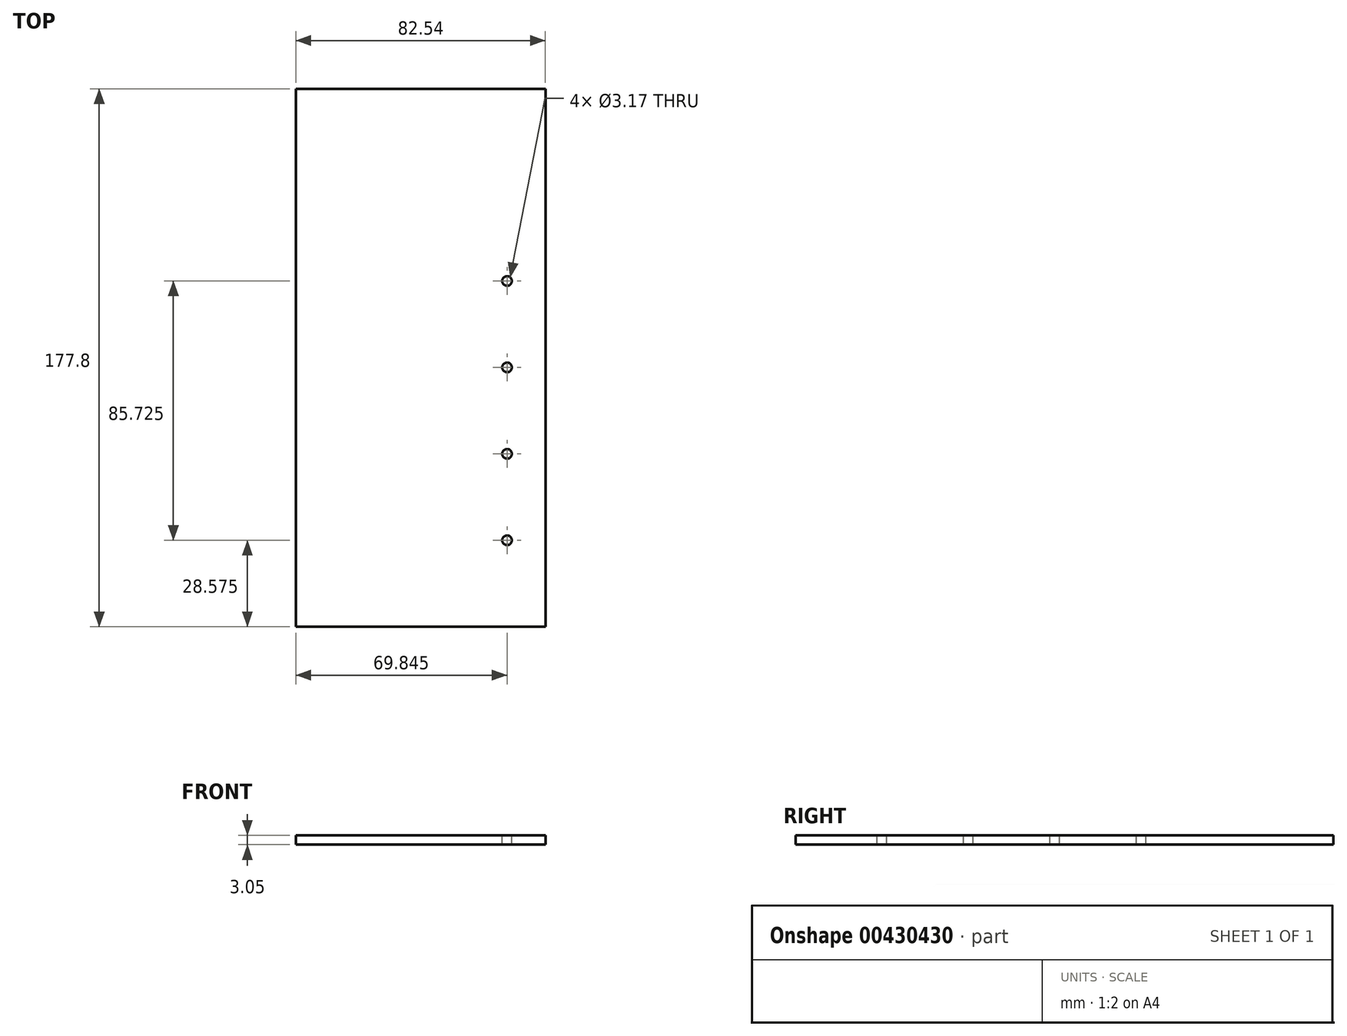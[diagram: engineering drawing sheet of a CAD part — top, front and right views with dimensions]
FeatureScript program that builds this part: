
annotation { "Feature Type Name" : "Feature", "Feature Type Description" : "" }
export const myFeature = defineFeature(function(context is Context, id is Id, definition is map)
    precondition{}
    {
        {
            var Q0;
            Q0=qCreatedBy(makeId("Top.planeOp"),FACE);
            var sketch = newSketch(context, id + "F0", { "sketchPlane" : qUnion([Q0])});
            skLineSegment(sketch, "E0.bottom", {"start": v(41.28, -88.9) * mm, "end": v(-41.27, -88.9) * mm});
            skLineSegment(sketch, "E0.top", {"start": v(41.27, 88.9) * mm, "end": v(-41.28, 88.9) * mm});
            skLineSegment(sketch, "E0.left", {"start": v(41.28, -88.9) * mm, "end": v(41.27, 88.9) * mm});
            skLineSegment(sketch, "E0.right", {"start": v(-41.27, -88.9) * mm, "end": v(-41.28, 88.9) * mm});
            skPoint(sketch, "E0.middle", {"position": v(0, 0) * mm});
            skSolve(sketch);
        }
        {
            var Q0;
            Q0=makeQuery(id+"F0.imprint","IMPRINT",FACE,{"disambiguationData":[TD([[makeQuery(id+"F0.imprint","IMPRINT",EDGE,{"derivedFrom":sQuery(id+"F0.wireOp",EDGE,"E0.bottom")}),-1.0]])]});
            extrude(context, id + "F1", {"entities" : qUnion([Q0]), "depth" : 3.05 * mm, "offsetDistance" : 25.4 * mm});
        }
        {
            var Q0;
            Q0=makeQuery(id+"F1.opExtrude","CAP_FACE",FACE,{"disambiguationData":[OSD([sQuery(id+"F0.wireOp",EDGE,"E0.bottom"),sQuery(id+"F0.wireOp",EDGE,"E0.top"),sQuery(id+"F0.wireOp",EDGE,"E0.left"),sQuery(id+"F0.wireOp",EDGE,"E0.right")])],"isStart":false});
            var sketch = newSketch(context, id + "F2", { "sketchPlane" : qUnion([Q0])});
            skLineSegment(sketch, "E1", {"start": v(28.57, 88.9) * mm, "end": v(28.58, -88.9) * mm, "construction": true});
            skCircle(sketch, "E2", {"center": v(28.58, -60.32) * mm, "radius": 1.59 * mm});
            skCircle(sketch, "E3.0.1.0", {"center": v(28.58, -31.75) * mm, "radius": 1.59 * mm});
            skCircle(sketch, "E3.0.2.0", {"center": v(28.58, -3.17) * mm, "radius": 1.59 * mm});
            skCircle(sketch, "E3.0.3.0", {"center": v(28.58, 25.4) * mm, "radius": 1.59 * mm});
            skLineSegment(sketch, "E3.direction1", {"start": v(28.58, -60.32) * mm, "end": v(53.98, -60.32) * mm, "construction": true});
            skLineSegment(sketch, "E3.direction2", {"start": v(28.58, -60.32) * mm, "end": v(28.58, -31.75) * mm, "construction": true});
            skLineSegment(sketch, "E4", {"start": v(28.57, 31.75) * mm, "end": v(41.27, 31.75) * mm, "construction": true});
            skSolve(sketch);
        }
        {
            var Q0;
            Q0=makeQuery(id+"F2.imprint","IMPRINT",FACE,{"disambiguationData":[TD([[makeQuery(id+"F2.imprint","IMPRINT",EDGE,{"derivedFrom":sQuery(id+"F2.wireOp",EDGE,"E3.0.4.0")}),1.0]])]});
            var Q1;
            Q1=makeQuery(id+"F2.imprint","IMPRINT",FACE,{"disambiguationData":[TD([[makeQuery(id+"F2.imprint","IMPRINT",EDGE,{"derivedFrom":sQuery(id+"F2.wireOp",EDGE,"E3.0.3.0")}),1.0]])]});
            var Q2;
            Q2=makeQuery(id+"F2.imprint","IMPRINT",FACE,{"disambiguationData":[TD([[makeQuery(id+"F2.imprint","IMPRINT",EDGE,{"derivedFrom":sQuery(id+"F2.wireOp",EDGE,"E3.0.2.0")}),1.0]])]});
            var Q3;
            Q3=makeQuery(id+"F2.imprint","IMPRINT",FACE,{"disambiguationData":[TD([[makeQuery(id+"F2.imprint","IMPRINT",EDGE,{"derivedFrom":sQuery(id+"F2.wireOp",EDGE,"E3.0.1.0")}),1.0]])]});
            var Q4;
            Q4=makeQuery(id+"F2.imprint","IMPRINT",FACE,{"disambiguationData":[TD([[makeQuery(id+"F2.imprint","IMPRINT",EDGE,{"derivedFrom":sQuery(id+"F2.wireOp",EDGE,"E2")}),1.0]])]});
            extrude(context, id + "F3", {"entities" : qUnion([Q0, Q1, Q2, Q3, Q4]), "operationType" : NewBodyOperationType.REMOVE, "oppositeDirection" : true, "depth" : 25.4 * mm, "offsetDistance" : 25.4 * mm});
        }
    });
